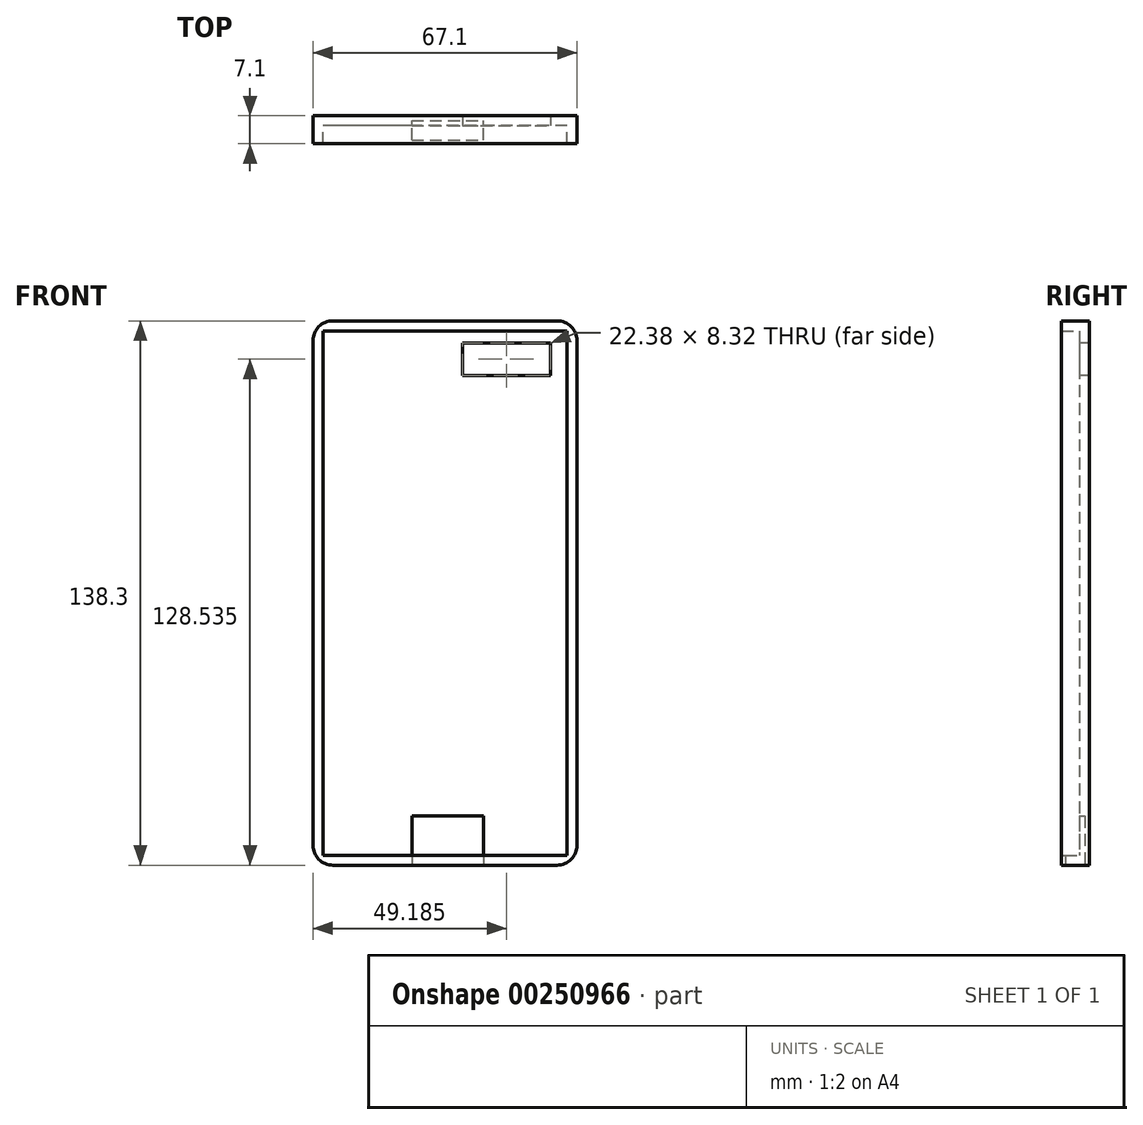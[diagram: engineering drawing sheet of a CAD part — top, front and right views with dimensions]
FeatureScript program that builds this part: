
annotation { "Feature Type Name" : "Feature", "Feature Type Description" : "" }
export const myFeature = defineFeature(function(context is Context, id is Id, definition is map)
    precondition{}
    {
        {
            var Q0;
            Q0=qCreatedBy(makeId("Front.planeOp"),FACE);
            var sketch = newSketch(context, id + "F0", { "sketchPlane" : qUnion([Q0])});
            skLineSegment(sketch, "E0.bottom", {"start": v(33.55, 69.15) * mm, "end": v(-33.55, 69.15) * mm});
            skLineSegment(sketch, "E0.top", {"start": v(33.55, -69.15) * mm, "end": v(-33.55, -69.15) * mm});
            skLineSegment(sketch, "E0.left", {"start": v(33.55, 69.15) * mm, "end": v(33.55, -69.15) * mm});
            skLineSegment(sketch, "E0.right", {"start": v(-33.55, 69.15) * mm, "end": v(-33.55, -69.15) * mm});
            skPoint(sketch, "E0.middle", {"position": v(0, 0) * mm});
            skSolve(sketch);
        }
        {
            var Q0;
            Q0=makeQuery(id+"F0.imprint","IMPRINT",FACE,{"disambiguationData":[TD([[makeQuery(id+"F0.imprint","IMPRINT",EDGE,{"derivedFrom":sQuery(id+"F0.wireOp",EDGE,"E0.bottom")}),1.0]])]});
            extrude(context, id + "F1", {"entities" : qUnion([Q0]), "depth" : 7.1 * mm});
        }
        {
            var Q0;
            Q0=makeQuery(id+"F1.opExtrude","CAP_FACE",FACE,{"disambiguationData":[OSD([sQuery(id+"F0.wireOp",EDGE,"E0.bottom"),sQuery(id+"F0.wireOp",EDGE,"E0.top"),sQuery(id+"F0.wireOp",EDGE,"E0.left"),sQuery(id+"F0.wireOp",EDGE,"E0.right")])],"isStart":false});
            shell(context, id + "F2", {"entities" : qUnion([Q0]), "thickness" : 2.54 * mm});
        }
        {
            var Q0;
            Q0=makeQuery(id+"F1.opExtrude","SWEPT_EDGE",EDGE,{"disambiguationData":[OSD([sQuery(id+"F0.wireOp",EDGE,"E0.bottom"),sQuery(id+"F0.wireOp",EDGE,"E0.left")])]});
            var Q1;
            Q1=makeQuery(id+"F1.opExtrude","SWEPT_EDGE",EDGE,{"disambiguationData":[OSD([sQuery(id+"F0.wireOp",EDGE,"E0.top"),sQuery(id+"F0.wireOp",EDGE,"E0.left")])]});
            var Q2;
            Q2=makeQuery(id+"F1.opExtrude","SWEPT_EDGE",EDGE,{"disambiguationData":[OSD([sQuery(id+"F0.wireOp",EDGE,"E0.bottom"),sQuery(id+"F0.wireOp",EDGE,"E0.right")])]});
            var Q3;
            Q3=makeQuery(id+"F1.opExtrude","SWEPT_EDGE",EDGE,{"disambiguationData":[OSD([sQuery(id+"F0.wireOp",EDGE,"E0.top"),sQuery(id+"F0.wireOp",EDGE,"E0.right")])]});
            fillet(context, id + "F3", {"entities" : qUnion([Q0, Q1, Q2, Q3]), "radius" : 5.08 * mm, "tangentPropagation" : true, "allowEdgeOverflow" : false});
        }
        {
            var Q0;
            Q0=makeQuery(id+"F2.opShell","OFFSET_FACE",FACE,{"disambiguationData":[OSD([sQuery(id+"F0.wireOp",EDGE,"E0.bottom"),sQuery(id+"F0.wireOp",EDGE,"E0.top"),sQuery(id+"F0.wireOp",EDGE,"E0.left"),sQuery(id+"F0.wireOp",EDGE,"E0.right")])]});
            var sketch = newSketch(context, id + "F4", { "sketchPlane" : qUnion([Q0])});
            skLineSegment(sketch, "E1.bottom", {"start": v(4.45, 63.55) * mm, "end": v(26.82, 63.55) * mm});
            skLineSegment(sketch, "E1.top", {"start": v(4.45, 55.23) * mm, "end": v(26.82, 55.23) * mm});
            skLineSegment(sketch, "E1.left", {"start": v(4.45, 63.55) * mm, "end": v(4.45, 55.23) * mm});
            skLineSegment(sketch, "E1.right", {"start": v(26.82, 63.55) * mm, "end": v(26.82, 55.23) * mm});
            skSolve(sketch);
        }
        {
            var Q0;
            Q0=makeQuery(id+"F1.opExtrude","SWEPT_FACE",FACE,{"disambiguationData":[OSD([sQuery(id+"F0.wireOp",EDGE,"E0.top")])]});
            var sketch = newSketch(context, id + "F5", { "sketchPlane" : qUnion([Q0])});
            skLineSegment(sketch, "E2.bottom", {"start": v(-8.42, 6.13) * mm, "end": v(9.8, 6.13) * mm});
            skLineSegment(sketch, "E2.top", {"start": v(-8.42, 1.17) * mm, "end": v(9.8, 1.17) * mm});
            skLineSegment(sketch, "E2.left", {"start": v(-8.42, 6.13) * mm, "end": v(-8.42, 1.17) * mm});
            skLineSegment(sketch, "E2.right", {"start": v(9.8, 6.13) * mm, "end": v(9.8, 1.17) * mm});
            skSolve(sketch);
        }
        {
            var Q0;
            Q0=makeQuery(id+"F5.imprint","IMPRINT",FACE,{"disambiguationData":[TD([[makeQuery(id+"F5.imprint","IMPRINT",EDGE,{"derivedFrom":sQuery(id+"F5.wireOp",EDGE,"E2.bottom")}),-1.0]])]});
            extrude(context, id + "F6", {"entities" : qUnion([Q0]), "operationType" : NewBodyOperationType.REMOVE, "endBound" : BoundingType.SYMMETRIC, "oppositeDirection" : true, "depth" : 25 * mm});
        }
        {
            var Q0;
            Q0=makeQuery(id+"F4.imprint","IMPRINT",FACE,{"disambiguationData":[TD([[makeQuery(id+"F4.imprint","IMPRINT",EDGE,{"derivedFrom":sQuery(id+"F4.wireOp",EDGE,"E1.bottom")}),-1.0]])]});
            extrude(context, id + "F7", {"entities" : qUnion([Q0]), "operationType" : NewBodyOperationType.REMOVE, "endBound" : BoundingType.SYMMETRIC, "oppositeDirection" : true, "depth" : 25 * mm});
        }
    });
